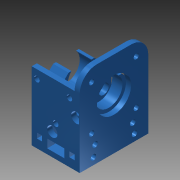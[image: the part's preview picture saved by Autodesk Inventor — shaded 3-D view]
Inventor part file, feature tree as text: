
AUTODESK INVENTOR PART (.ipt)
format: ipt  version: 2013 SP2 (Build 170200200, 200)  size: 452,608 bytes
history: native  units: mm
features: extrude x16, sketch x12, reference x10, projected_geometry x9, chamfer x2, fillet x1
ambient origin geometry x8: Origin, YZ Plane, XZ Plane, XY Plane, X Axis, Y Axis, Z Axis, Center Point
bodies: Solid1 (feature_tree)
feature tree (50):
  sketch  "Sketch1"  dims[d0=28.0mm d1=40.0mm]
  extrude  "Extrusion1"  Depth=40.0mm
  extrude  "Extrusion3"  Depth=10.0mm
  extrude  "Extrusion4"  Depth=3.0mm
  extrude  "Extrusion6"  Depth=3.0mm
  extrude  "Extrusion7"  Depth=50.0mm TaperAngle=0.0deg
  extrude  "Extrusion8"  Depth=15.0mm TaperAngle=0.0deg
  extrude  "Extrusion9"  Depth=3.2mm
  extrude  "Extrusion10"  Depth=24.0mm
  extrude  "Extrusion11"  Depth=4.0mm
  chamfer  "Chamfer1"  Distance=3.0mm
  extrude  "Extrusion12"  Depth=5.0mm TaperAngle=0.0deg
  extrude  "Extrusion13"  Depth=3.2mm
  fillet  "Fillet1"  Radius=3.2mm
  chamfer  "Chamfer2"  Distance=9.0mm
  extrude  "Extrusion14"  Depth=5.0mm
  extrude  "Extrusion15"  Depth=5.0mm
  extrude  "Extrusion16"  Depth=9.0mm
  extrude  "Extrusion17"  Depth=6.0mm
  extrude  "Extrusion18"  Depth=6.0mm
  sketch  "Sketch7"  dims[d2=3.0mm d3=0.0mm d15=10.0mm]
  sketch  "Sketch9"  dims[d16=40.0mm d18=3.0mm]
  sketch  "Sketch10"  dims[d19=3.0mm d20=3.0mm]
  sketch  "Sketch11"  dims[d22=15.0mm d23=0.0mm d24=50.0mm d25=0.0mm]
  projected_geometry  "Projected Loop1"
  projected_geometry  "Projected Loop2"
  projected_geometry  "Projected Loop3"
  projected_geometry  "Projected Loop4"
  projected_geometry  "Projected Loop5"
  projected_geometry  "Projected Loop6"
  sketch  "Sketch12"  dims[d30=8.0mm d31=15.0mm d32=0.0mm]
  projected_geometry  "Projected Loop7"
  sketch  "Sketch13"  dims[d33=3.0mm d34=3.2mm]
  reference  "Reference2"
  sketch  "Sketch14"  dims[d35=3.2mm d36=24.0mm]
  reference  "Reference3"
  reference  "Reference4"
  reference  "Reference5"
  reference  "Reference6"
  reference  "Reference7"
  reference  "Reference8"
  sketch  "Sketch15"  dims[d37=0.0mm d38=0.0mm d40=4.0mm]
  sketch  "Sketch17"  dims[d41=6.0mm]
  reference  "Reference10"
  sketch  "Sketch18"  dims[d43=5.5mm]
  projected_geometry  "Projected Loop8"
  projected_geometry  "Projected Loop9"
  sketch  "Sketch19"  dims[d44=3.0mm d45=3.0mm d46=5.0mm d47=0.0mm d48=3.2mm d49=3.2mm d50=9.0mm d51=5.0mm d52=5.0mm d53=9.0mm d54=6.0mm d55=6.0mm d56=3.0mm d57=0.0mm d58=2.0mm d59=0.0mm d60=35.0mm d63=20.0mm d64=0.0mm d65=10.0mm d66=2.0mm d67=45.0deg d68=16.0mm d70=30.0mm d71=0.0mm d72=3.0mm d73=0.0mm d74=10.0mm d75=2.0mm d76=2.0mm d77=45.0deg d78=8.0mm d79=3.0mm d80=0.0mm d81=3.2mm d82=3.2mm d83=3.2mm d84=35.0mm d85=3.0mm d86=6.0mm d87=18.0mm d88=3.0mm d89=0.0mm d91=2.5mm d92=8.0mm d93=0.0mm d94=2.5mm d96=4.0mm d98=5.0mm d99=0.0mm d100=6.0mm d101=6.0mm d102=0.0mm d103=0.0mm d104=6.0mm d105=6.0mm d107=0.5mm]
  reference  "Reference13"
  reference  "Reference14"
